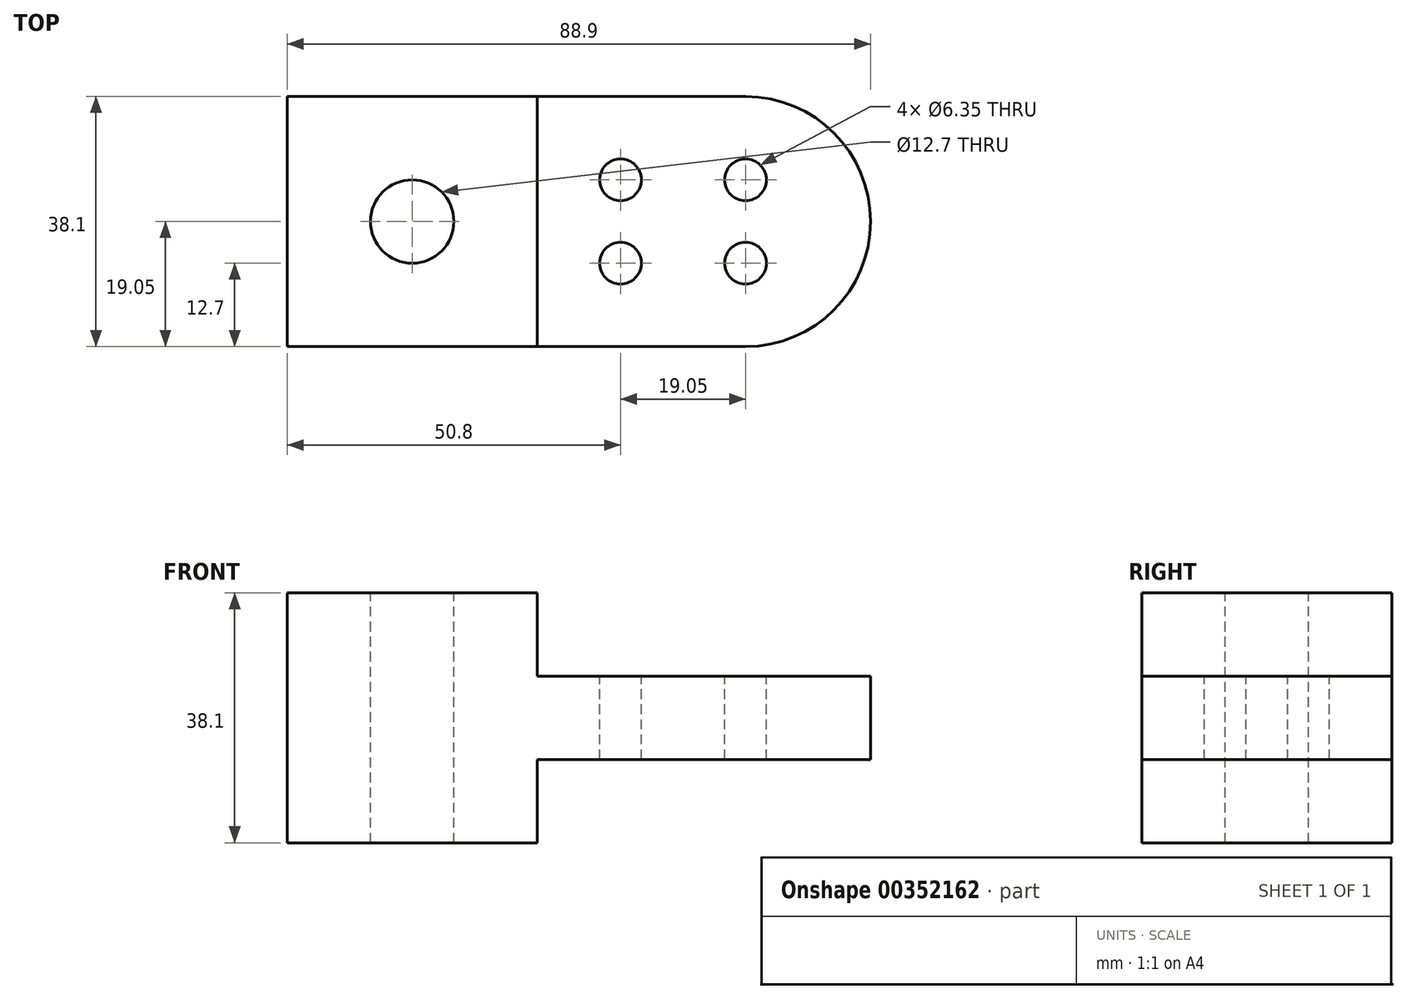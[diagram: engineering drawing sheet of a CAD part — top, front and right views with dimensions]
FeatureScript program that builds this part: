
annotation { "Feature Type Name" : "Feature", "Feature Type Description" : "" }
export const myFeature = defineFeature(function(context is Context, id is Id, definition is map)
    precondition{}
    {
        {
            var Q0;
            Q0=qCreatedBy(makeId("Top.planeOp"),FACE);
            var sketch = newSketch(context, id + "F0", { "sketchPlane" : qUnion([Q0])});
            skLineSegment(sketch, "E0", {"start": v(0, 0) * mm, "end": v(0, 38.1) * mm});
            skLineSegment(sketch, "E1", {"start": v(0, 38.1) * mm, "end": v(38.1, 38.1) * mm});
            skLineSegment(sketch, "E2", {"start": v(38.1, 38.1) * mm, "end": v(38.1, 0) * mm});
            skLineSegment(sketch, "E3", {"start": v(38.1, 0) * mm, "end": v(0, 0) * mm});
            skSolve(sketch);
        }
        {
            var Q0;
            Q0 = qSketchRegion(id + "F0", true);
            extrude(context, id + "F1", {"entities" : qUnion([Q0]), "endBound" : BoundingType.SYMMETRIC, "depth" : 38.1 * mm});
        }
        {
            var Q0;
            Q0=makeQuery(id+"F1.opExtrude","CAP_FACE",FACE,{"disambiguationData":[OSD([sQuery(id+"F0.wireOp",EDGE,"E0"),sQuery(id+"F0.wireOp",EDGE,"E1"),sQuery(id+"F0.wireOp",EDGE,"E2"),sQuery(id+"F0.wireOp",EDGE,"E3")])],"isStart":false});
            var sketch = newSketch(context, id + "F2", { "sketchPlane" : qUnion([Q0])});
            skCircle(sketch, "E4", {"center": v(19.05, 19.05) * mm, "radius": 6.35 * mm});
            skSolve(sketch);
        }
        {
            var Q0;
            Q0 = qSketchRegion(id + "F2", true);
            extrude(context, id + "F3", {"entities" : qUnion([Q0]), "operationType" : NewBodyOperationType.REMOVE, "endBound" : BoundingType.THROUGH_ALL, "oppositeDirection" : true, "depth" : 25.4 * mm});
        }
        {
            var Q0;
            Q0=qCreatedBy(makeId("Top.planeOp"),FACE);
            var sketch = newSketch(context, id + "F4", { "sketchPlane" : qUnion([Q0])});
            skLineSegment(sketch, "E5", {"start": v(38.1, 38.1) * mm, "end": v(69.85, 38.1) * mm});
            skLineSegment(sketch, "E6", {"start": v(38.1, 0) * mm, "end": v(69.85, 0) * mm});
            skArc(sketch, "E7", {"start": v(69.85, 0) * mm, "mid": v(88.9, 19.05) * mm, "end": v(69.85, 38.1) * mm});
            skLineSegment(sketch, "E8", {"start": v(38.1, 38.1) * mm, "end": v(38.1, 0) * mm});
            skSolve(sketch);
        }
        {
            var Q0;
            Q0 = qSketchRegion(id + "F4", true);
            extrude(context, id + "F5", {"entities" : qUnion([Q0]), "operationType" : NewBodyOperationType.ADD, "endBound" : BoundingType.SYMMETRIC, "depth" : 12.7 * mm});
        }
        {
            var Q0;
            Q0=makeQuery(id+"F5.opExtrude","CAP_FACE",FACE,{"disambiguationData":[OSD([sQuery(id+"F4.wireOp",EDGE,"E5"),sQuery(id+"F4.wireOp",EDGE,"E6"),sQuery(id+"F4.wireOp",EDGE,"E7"),sQuery(id+"F4.wireOp",EDGE,"E8")])],"isStart":false});
            var sketch = newSketch(context, id + "F6", { "sketchPlane" : qUnion([Q0])});
            skLineSegment(sketch, "E9", {"start": v(38.1, 19.05) * mm, "end": v(98.49, 19.05) * mm, "construction": true});
            skCircle(sketch, "E10", {"center": v(50.8, 25.4) * mm, "radius": 3.18 * mm});
            skCircle(sketch, "E11", {"center": v(69.85, 25.4) * mm, "radius": 3.18 * mm});
            skCircle(sketch, "E12.MirrorC", {"center": v(50.8, 12.7) * mm, "radius": 3.18 * mm});
            skCircle(sketch, "E13.MirrorC", {"center": v(69.85, 12.7) * mm, "radius": 3.18 * mm});
            skSolve(sketch);
        }
        {
            var Q0;
            Q0 = qSketchRegion(id + "F6", true);
            extrude(context, id + "F7", {"entities" : qUnion([Q0]), "operationType" : NewBodyOperationType.REMOVE, "endBound" : BoundingType.THROUGH_ALL, "oppositeDirection" : true, "depth" : 25.4 * mm});
        }
    });
